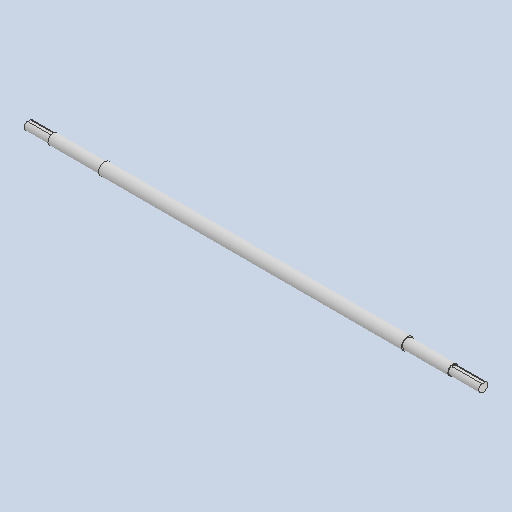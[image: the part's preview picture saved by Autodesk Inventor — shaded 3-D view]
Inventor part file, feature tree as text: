
AUTODESK INVENTOR PART (.ipt)
format: ipt  version: 2024 (Build 280153000, 153)  size: 89,088 bytes
history: native  units: in
note: dims shown in document units (in); Inventor stores cm internally (conversion verified against a paired STEP export)
features: fillet x1
ambient origin geometry x8: Origin, YZ Plane, XZ Plane, XY Plane, X Axis, Y Axis, Z Axis, Center Point
bodies: Solid1 (feature_tree)
feature tree (1):
  fillet  "Fillet2"  [1 undecoded]
note: 1 required parameter value undecoded (feature->parameter linkage not recoverable at this tier; creation-order binding heuristic only, values carry confidence <= 0.55)
